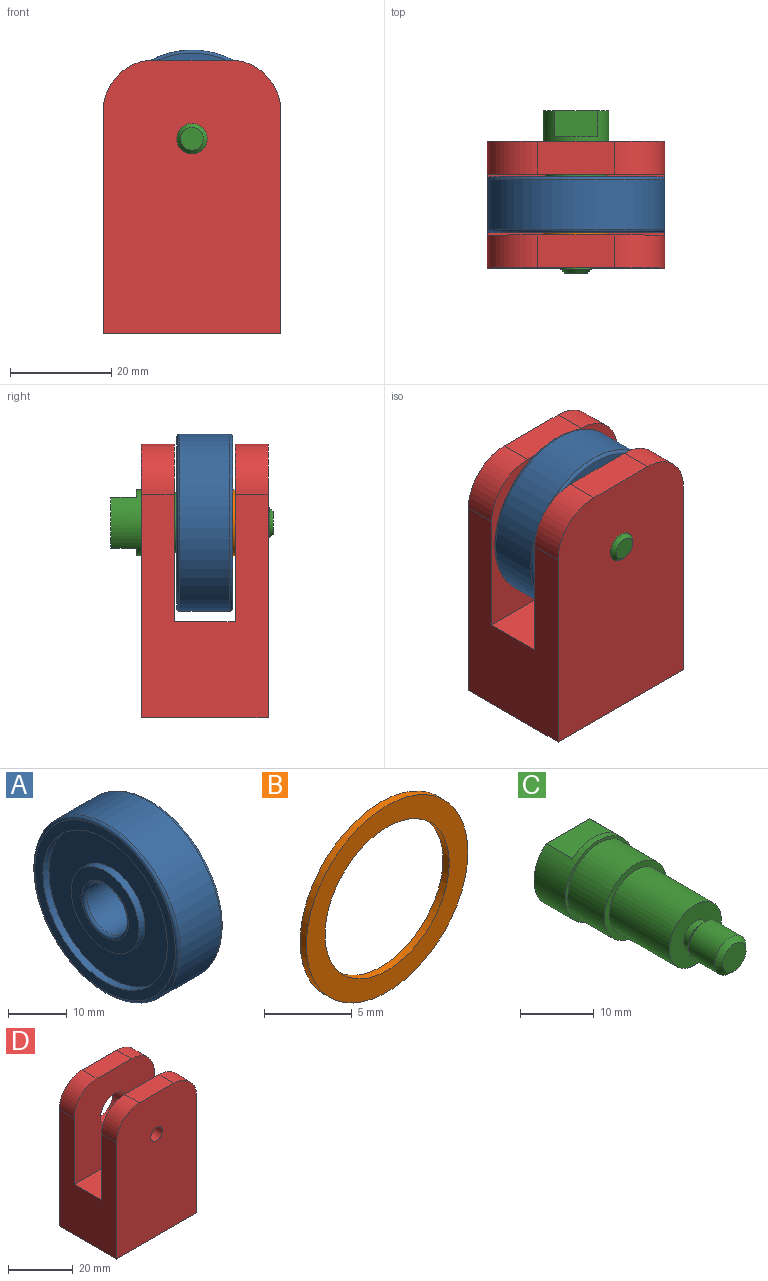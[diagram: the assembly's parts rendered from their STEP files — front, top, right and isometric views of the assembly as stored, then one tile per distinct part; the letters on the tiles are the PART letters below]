
ASSEMBLY  parts=4 mates=3
PART A: 16 faces, bbox 11x37.9x37.9 mm
  f0: plane 16.3x16.3mm, normal (-1,0,0), area 110.2mm2, adj f1,f15
  f1: torus R=5.6mm, axis (1,0,0), area 30.9mm2, adj f0,f2
  f2: cylinder r=5mm len=10mm, axis (1,0,0), area 307.9mm2, adj f1,f3
  f3: torus R=5.6mm, axis (1,0,0), area 30.9mm2, adj f2,f4
  f4: plane 16.3x16.3mm, normal (1,0,0), area 110.2mm2, adj f3,f5
  f5: cylinder r=8.15mm len=16.3mm, axis (1,0,0), area 73.4mm2, adj f4,f6
  f6: plane 29.9x29.9mm, normal (1,0,0), area 493.5mm2, adj f5,f7
  f7: cylinder r=14.95mm len=29.9mm, axis (1,0,0), area 134.6mm2, adj f6,f8
  f8: plane 33.8x33.8mm, normal (1,0,0), area 195.1mm2, adj f7,f9
  f9: torus R=16.9mm, axis (1,0,0), area 102.3mm2, adj f8,f10
  f10: cylinder r=17.5mm len=35mm, axis (1,0,0), area 1077.6mm2, adj f9,f11
  f11: torus R=16.9mm, axis (1,0,0), area 102.3mm2, adj f10,f12
  f12: plane 33.8x33.8mm, normal (-1,0,0), area 195.1mm2, adj f11,f13
  f13: cylinder r=14.95mm len=29.9mm, axis (1,0,0), area 134.6mm2, adj f12,f14
  f14: plane 29.9x29.9mm, normal (-1,0,0), area 493.5mm2, adj f13,f15
  f15: cylinder r=8.15mm len=16.3mm, axis (1,0,0), area 73.4mm2, adj f0,f14
PART B: 4 faces, bbox 13x0.5x13 mm
  f0: cylinder r=5mm len=10mm, axis (0,1,0), area 15.7mm2, adj f1,f3
  f1: plane 13x13mm, normal (0,1,0), area 54.2mm2, adj f0,f2
  f2: cylinder r=6.5mm len=13mm, axis (0,1,0), area 20.4mm2, adj f1,f3
  f3: plane 13x13mm, normal (0,-1,0), area 54.2mm2, adj f0,f2
PART C: 16 faces, bbox 13x32x13 mm
  f0: plane 13x10mm, normal (0,1,0), area 115.7mm2, adj f8,f12,f14
  f1: cylinder r=5mm len=11.5mm, axis (0,1,0), area 361.3mm2, adj f2,f11
  f2: plane 10x10mm, normal (0,-1,0), area 62.6mm2, adj f1,f3
  f3: cylinder r=2.25mm len=4.5mm, axis (0,1,0), area 14.1mm2, adj f2,f4
  f4: cone r=2.25mm half-angle=45deg, axis (0,-1,0), area 17.5mm2, adj f3,f5
  f5: cylinder r=3mm len=6mm, axis (0,1,0), area 94.2mm2, adj f4,f6
  f6: cone r=3mm half-angle=45deg, axis (0,1,0), area 17.5mm2, adj f5,f7
  f7: plane 4.5x4.5mm, normal (0,-1,0), area 15.9mm2, adj f6
  f8: cylinder r=6.5mm len=13mm, axis (0,1,0), area 154.9mm2, adj f0,f9,f12,f13,f14,f15
  f9: plane 13x13mm, normal (0,-1,0), area 19.6mm2, adj f8,f10
  f10: cylinder r=6mm len=12mm, axis (0,1,0), area 263.9mm2, adj f9,f11
  f11: plane 12x12mm, normal (0,-1,0), area 34.6mm2, adj f1,f10
  f12: plane 8.31x5mm, normal (0,0,-1), area 41.5mm2, adj f0,f8,f13
  f13: plane 8.31x1.5mm, normal (0,1,0), area 8.5mm2, adj f8,f12
  f14: plane 8.31x5mm, normal (0,0,1), area 41.5mm2, adj f0,f8,f15
  f15: plane 8.31x1.5mm, normal (0,1,0), area 8.5mm2, adj f8,f14
PART D: 20 faces, bbox 35x25x54 mm
  f0: plane 15x6.5mm, normal (0,0,1), area 97.5mm2, adj f5,f8,f14,f15
  f1: plane 15x6.5mm, normal (0,0,1), area 97.5mm2, adj f4,f7,f12,f13
  f2: plane 44x25mm, normal (-1,0,0), area 800mm2, adj f3,f4,f5,f7,f8,f9,f12,f14
  f3: plane 35x25mm, normal (0,0,-1), area 835.7mm2, adj f2,f4,f5,f6,f17,f19
  f4: plane 54x35mm, normal (0,-1,0), area 1827.4mm2, adj f1,f2,f3,f6,f11,f12,f13
  f5: plane 54x35mm, normal (0,1,0), area 1734mm2, adj f0,f2,f3,f6,f10,f14,f15
  f6: plane 44x25mm, normal (1,0,0), area 800mm2, adj f3,f4,f5,f7,f8,f9,f13,f15
  f7: plane 35x35mm, normal (0,1,0), area 1162.4mm2, adj f1,f2,f6,f9,f11,f12,f13
  f8: plane 35x35mm, normal (0,-1,0), area 1069mm2, adj f0,f2,f6,f9,f10,f14,f15
  f9: plane 35x12mm, normal (0,0,1), area 420mm2, adj f2,f6,f7,f8
  f10: cylinder r=6mm len=12mm, axis (0,1,0), area 245mm2, adj f5,f8
  f11: cylinder r=2.5mm len=6.5mm, axis (0,1,0), area 102.1mm2, adj f4,f7
  f12: cylinder r=10mm len=10mm, axis (0,1,0), area 102.1mm2, adj f1,f2,f4,f7
  f13: cylinder r=10mm len=10mm, axis (0,-1,0), area 102.1mm2, adj f1,f4,f6,f7
  f14: cylinder r=10mm len=10mm, axis (0,1,0), area 102.1mm2, adj f0,f2,f5,f8
  f15: cylinder r=10mm len=10mm, axis (0,-1,0), area 102.1mm2, adj f0,f5,f6,f8
  f16: cone r=0mm half-angle=59deg, axis (0,0,-1), area 22.9mm2, adj f17
  f17: cylinder r=2.5mm len=11mm, axis (0,0,-1), area 172.8mm2, adj f3,f16
  f18: cone r=0mm half-angle=59deg, axis (0,0,-1), area 22.9mm2, adj f19
  f19: cylinder r=2.5mm len=11mm, axis (0,0,-1), area 172.8mm2, adj f3,f18
PLACE A rot(axis=(0.58,-0.58,-0.58),120deg) t=(-10,5.5,38.5)mm
PLACE B t=(-10,-210,0)mm
PLACE C t=(-10,-210,0)mm
PLACE D t=(-10,-210,0)mm
MATE fastened D.f11 <-> B.f0  axis (0,1,0) through (-10,-6,38.5)mm
MATE revolute A.f1 <-> D.f11  axis (0,-1,0) through (-10,-5.5,38.5)mm
MATE fastened C.f1 <-> D.f11  axis (0,-1,0) through (-10,-6,38.5)mm
